# Revit family: CAD-FL
name_source: partatom
category: Generic Models
revit_build: Autodesk Revit 2018 (Build: 20170223_1515(x64)
units: mm (PartAtom-declared; Revit-internal decimal feet)

## family parameters
Can host rebar = No
Cut with Voids When Loaded = No
Host = Face
Part Type = Normal
Room Calculation Point = No
Round Connector Dimension = Use Diameter
Shared = No

## types (19) — shared parameters
Default Elevation = 4' - 0"
Description = CEILING OR WALL ACCESS DOOR,FLUSH DOOR WITH FRAME
Manufacturer = MIFAB
Material = <By Category>
Model = CAD-FL
URL = WWW.MIFAB.COM

## per-type parameters (varying)
| type | Height | Width |
| CAD-FL-8"x8" | 0' - 8" | 0' - 8" |
| CAD-FL-8"12" | 1' - 0" | 0' - 8" |
| CAD-FL-10"x10" | 0' - 10" | 0' - 10" |
| CAD-FL-12"x12" | 1' - 0" | 1' - 0" |
| CAD-FL-12"x16" | 1' - 4" | 1' - 0" |
| CAD-FL-12"x18" | 1' - 6" | 1' - 0" |
| CAD-FL-12"x24" | 2' - 0" | 1' - 0" |
| CAD-FL-14"x14" | 1' - 2" | 1' - 2" |
| CAD-FL-16"x16" | 1' - 4" | 1' - 4" |
| CAD-FL-16"x20" | 1' - 8" | 1' - 4" |
| CAD-FL-18"x18" | 1' - 6" | 1' - 6" |
| CAD-FL-20"x24" | 2' - 0" | 1' - 8" |
| CAD-FL-20"x30" | 2' - 6" | 1' - 8" |
| CAD-FL-24"x24" | 2' - 0" | 2' - 0" |
| CAD-FL-24"x30" | 2' - 6" | 2' - 0" |
| CAD-FL-24"x36" | 3' - 0" | 2' - 0" |
| CAD-FL-30"x30" | 2' - 6" | 2' - 6" |
| CAD-FL-36"x36" | 3' - 0" | 3' - 0" |
| CAD-FL-18"x24" | 2' - 0" | 1' - 6" |

## geometry (parser evidence)
native form markers: Sweep x5
no freeform markers — native parametric forms only
